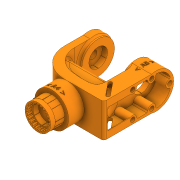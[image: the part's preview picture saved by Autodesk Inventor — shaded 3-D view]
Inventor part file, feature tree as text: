
AUTODESK INVENTOR PART (.ipt)
format: ipt  version: 2020 (Build 240168000, 168)  size: 2,288,128 bytes
history: native  units: in
note: dims shown in document units (in); Inventor stores cm internally (conversion verified against a paired STEP export)
features: sketch x47, extrude x43, projected_geometry x37, fillet x10, chamfer x9, plane x8, emboss x3
ambient origin geometry x8: Origin, YZ Plane, XZ Plane, XY Plane, X Axis, Y Axis, Z Axis, Center Point
bodies: Solid1 (feature_tree)
feature tree (157):
  extrude  "Extrusion1"  Depth=2.0472in
  extrude  "Extrusion2"  Depth=1.1063in
  chamfer  "Chamfer2"  Distance=0.5591in
  extrude  "Extrusion4"  Depth=0.0157in
  extrude  "Extrusion7"  Depth=0.2756in TaperAngle=0.0deg
  chamfer  "Chamfer4"  Distance=0.0394in
  extrude  "Extrusion8"  Depth=0.0157in
  sketch  "Sketch12"  dims[d39=1.4567in d57=0.0394in d58=0.0in]
  plane  "Work Plane1"
  sketch  "Sketch13"  dims[d59=0.315in d60=0.125in d61=0.0137in d67=0.0157in]
  extrude  "Extrusion10"  Depth=0.0394in TaperAngle=0.0deg
  extrude  "Extrusion11"  Depth=0.0866in
  chamfer  "Chamfer5"  Distance=9.4488in Angle=360.0deg
  extrude  "Extrusion12"  Depth=0.2756in TaperAngle=0.0deg
  plane  "Work Plane2"
  extrude  "Extrusion13"  Depth=0.315in
  plane  "Work Plane3"
  extrude  "Extrusion14"  Depth=1.0236in
  extrude  "Extrusion15"  Depth=0.8858in
  extrude  "Extrusion16"  Depth=0.3937in
  extrude  "Extrusion17"  Depth=1.378in
  sketch  "Sketch21"  dims[d107=0.315in d108=0.0in d109=0.315in d110=0.125in d111=0.0137in]
  extrude  "Extrusion19"  Depth=0.5906in
  sketch  "Sketch23"  dims[d112=1.0in d113=0.0in d114=1.0236in]
  extrude  "Extrusion20"  Depth=0.1575in TaperAngle=0.0deg
  extrude  "Extrusion21"  Depth=0.1575in TaperAngle=0.0deg
  extrude  "Extrusion22"  Depth=4.2323in
  extrude  "Extrusion23"  Depth=0.1575in
  extrude  "Extrusion24"  Depth=1.1024in
  extrude  "Extrusion25"  Depth=0.4921in
  extrude  "Extrusion26"  Depth=0.75in
  extrude  "Extrusion27"  Depth=0.2165in TaperAngle=0.0deg
  extrude  "Extrusion28"  Depth=0.1575in
  extrude  "Extrusion29"  Depth=0.1575in
  plane  "Work Plane4"
  extrude  "Extrusion30"  Depth=0.3937in TaperAngle=0.0deg
  fillet  "Fillet1"  Radius=0.3937in
  fillet  "Fillet2"  Radius=0.315in
  extrude  "Extrusion31"  Depth=0.315in TaperAngle=0.0deg
  extrude  "Extrusion32"  Depth=0.315in TaperAngle=0.0deg
  extrude  "Extrusion33"  Depth=0.3937in TaperAngle=0.0deg
  fillet  "Fillet3"  Radius=0.2165in
  extrude  "Extrusion34"  Depth=0.4724in
  chamfer  "Chamfer6"  Distance=0.2756in
  chamfer  "Chamfer7"  Distance=0.0394in
  extrude  "Extrusion35"  Depth=0.0394in
  extrude  "Extrusion36"  Depth=0.1575in TaperAngle=0.0deg
  fillet  "Fillet5"  Radius=0.1575in
  extrude  "Extrusion38"  Depth=0.315in
  extrude  "Extrusion39"  Depth=0.0157in
  extrude  "Extrusion40"  Depth=1.0in TaperAngle=0.0deg
  extrude  "Extrusion41"  Depth=0.3937in
  chamfer  "Chamfer8"  Distance=0.3937in
  extrude  "Extrusion42"  Depth=0.1575in
  plane  "Work Plane6"
  emboss  "Emboss1"
  emboss  "Emboss2"
  plane  "Work Plane7"
  emboss  "Emboss3"
  extrude  "Extrusion43"  Depth=0.1181in
  fillet  "Fillet9"  Radius=1.0039in
  chamfer  "Chamfer10"  Distance=0.0984in
  extrude  "Extrusion44"  Depth=0.0394in
  extrude  "Extrusion45"  Depth=0.0394in
  fillet  "Fillet12"  Radius=0.1181in
  fillet  "Fillet13"  Radius=0.2047in
  plane  "Work Plane8"
  extrude  "Extrusion46"  Depth=0.0394in
  plane  "Work Plane9"
  extrude  "Extrusion47"  TaperAngle=0.0deg  [1 undecoded]
  fillet  "Fillet14"  Radius=0.0787in
  extrude  "Extrusion48"  Depth=0.0394in
  extrude  "Extrusion49"  Depth=0.0394in
  chamfer  "Chamfer11"  Distance=0.0787in
  chamfer  "Chamfer12"  Distance=0.2756in
  fillet  "Fillet15"  Radius=0.2756in
  fillet  "Fillet16"  Radius=0.4724in
  sketch  "Sketch1"  dims[d0=0.6299in d1=2.0472in]
  sketch  "Sketch2"  dims[d2=0.9449in d3=0.0in d4=1.1063in]
  sketch  "Sketch4"  dims[d5=1.5748in d6=0.5591in d7=0.0in]
  sketch  "Sketch8"  dims[d11=0.5591in d12=0.125in d13=0.0137in d25=0.0157in]
  projected_geometry  "Projected Loop2"
  sketch  "Sketch10"  dims[d26=6.2992in d28=360.0deg d30=0.2756in d31=0.0in]
  sketch  "Sketch14"  dims[d68=4.7244in d70=360.0deg d72=0.0394in d73=0.0in]
  sketch  "Sketch15"  dims[d83=0.0591in d84=0.0866in]
  projected_geometry  "Projected Loop4"
  sketch  "Sketch16"  dims[d85=0.0827in]
  sketch  "Sketch17"  dims[d86=0.0827in]
  projected_geometry  "Projected Loop5"
  sketch  "Sketch18"  dims[d87=0.0827in d88=9.4488in d90=360.0deg]
  projected_geometry  "Projected Loop6"
  projected_geometry  "Projected Loop7"
  sketch  "Sketch19"  dims[d92=0.2756in]
  projected_geometry  "Projected Loop8"
  projected_geometry  "Projected Loop9"
  sketch  "Sketch20"  dims[d94=9.4488in d95=0.0827in d96=0.0827in d97=0.0827in d98=360.0deg d105=0.2756in d106=0.0in]
  projected_geometry  "Projected Loop10"
  projected_geometry  "Projected Loop11"
  projected_geometry  "Projected Loop12"
  projected_geometry  "Projected Loop13"
  sketch  "Sketch25"  dims[d115=0.7874in d117=0.8858in]
  sketch  "Sketch26"  dims[d118=2.7559in d119=0.3937in]
  projected_geometry  "Projected Loop16"
  projected_geometry  "Projected Loop17"
  sketch  "Sketch27"  dims[d120=0.5906in d121=1.378in]
  projected_geometry  "Projected Loop18"
  projected_geometry  "Projected Loop19"
  sketch  "Sketch28"  dims[d123=3.4941in d124=0.5906in]
  projected_geometry  "Projected Loop20"
  projected_geometry  "Projected Loop21"
  sketch  "Sketch29"  dims[d126=1.9685in d129=0.1575in d130=0.0in]
  projected_geometry  "Projected Loop22"
  projected_geometry  "Projected Loop23"
  sketch  "Sketch30"  dims[d131=-2.0472in d132=0.1575in d133=0.0in]
  projected_geometry  "Projected Loop24"
  sketch  "Sketch31"  dims[d134=2.126in d136=4.2323in]
  sketch  "Sketch32"  dims[d137=0.1575in d138=0.1575in]
  sketch  "Sketch34"  dims[d139=0.4921in d140=0.0in d141=1.1024in]
  projected_geometry  "Projected Loop25"
  sketch  "Sketch35"  dims[d142=1.1614in d143=0.4921in]
  sketch  "Sketch36"  dims[d144=0.3445in d145=0.75in]
  projected_geometry  "Projected Loop26"
  sketch  "Sketch37"  dims[d146=0.1575in d147=0.0in d148=0.2165in d149=0.0in]
  projected_geometry  "Projected Loop27"
  sketch  "Sketch38"  dims[d152=1.0039in d153=0.0in d154=0.1575in]
  projected_geometry  "Projected Loop28"
  sketch  "Sketch39"  dims[d155=0.1575in d160=1.1811in]
  projected_geometry  "Projected Loop29"
  sketch  "Sketch40"  dims[d161=0.1969in d162=0.0in d163=0.315in d164=0.0in d165=0.3937in d166=0.0in d167=0.315in d168=0.0in]
  sketch  "Sketch41"  dims[d169=0.315in d170=0.0in d171=0.315in d172=0.0in]
  projected_geometry  "Projected Loop30"
  sketch  "Sketch43"  dims[d173=0.315in d174=0.0in d175=0.315in d176=0.0in]
  projected_geometry  "Projected Loop31"
  sketch  "Sketch44"  dims[d177=1.1024in d178=0.3937in d179=0.0in d180=0.2165in d181=0.0in]
  sketch  "Sketch45"  dims[d183=-0.0197in d184=0.4724in d185=0.2756in d186=0.0in]
  sketch  "Sketch46"  dims[d187=0.5512in]
  projected_geometry  "Projected Loop32"
  sketch  "Sketch47"  dims[d188=0.2165in d189=0.0394in d190=0.0in]
  projected_geometry  "Projected Loop33"
  sketch  "Sketch48"  dims[d191=0.0394in d192=0.0in d193=0.001in]
  sketch  "Sketch49"  dims[d194=0.001in d195=1.0in d196=0.0in d197=0.1575in]
  sketch  "Sketch50"  dims[d198=1.0in d199=0.0in d200=0.315in d201=0.125in d202=0.0137in]
  sketch  "Sketch52"  dims[d203=0.315in d204=0.125in d205=0.0137in d206=0.0157in]
  sketch  "Sketch53"  dims[d207=2.3622in d209=360.0deg d211=1.0in d212=0.0in]
  projected_geometry  "Projected Loop35"
  projected_geometry  "Projected Loop36"
  projected_geometry  "Projected Loop37"
  projected_geometry  "Projected Loop38"
  projected_geometry  "Projected Loop39"
  sketch  "Sketch54"  dims[d213=1.0in d214=0.0in d221=0.1969in d222=0.3937in d223=0.0in]
  projected_geometry  "Projected Loop40"
  sketch  "Sketch56"  dims[d224=0.1575in d225=0.0787in]
  sketch  "Sketch57"  dims[d226=0.1969in d227=0.0in d229=0.1181in d230=1.0039in]
  sketch  "Sketch59"  dims[d231=0.4134in]
  projected_geometry  "Projected Loop41"
  sketch  "Sketch60"  dims[d232=0.5118in d233=0.0984in d235=0.0197in d236=0.1181in d237=0.1181in d238=0.2047in d239=0.2047in d240=0.0in d241=0.0in d243=0.0787in d244=0.0787in d251=0.0787in d252=0.0787in d253=0.2756in d254=0.4724in d255=0.2756in d256=0.4724in d257=0.2756in d258=0.4724in d259=0.2756in d260=0.4724in d261=0.1575in d262=0.0in d263=0.0787in d264=0.125in d265=45.0deg d266=1.0in d267=0.0in d269=0.0394in d270=0.0in d271=0.0394in d272=0.0in d273=0.0394in d274=0.0in d275=0.0039in d276=0.0787in d277=1.0in d278=0.0in d279=0.122in d282=0.1378in d283=0.2047in d288=0.0394in d289=0.125in d290=45.0deg d291=0.5709in d292=0.0in d293=0.2835in d294=0.0in d295=0.2361in d296=0.0315in d297=1.1811in d298=0.315in d299=0.0984in d300=0.0in d301=0.0984in d302=0.0984in d303=0.0in d304=0.0256in d305=0.2559in d306=0.0in d307=0.2559in d308=0.0in d309=0.1181in d310=0.1969in d311=45.0deg d312=0.1181in d313=0.1969in d314=45.0deg d315=0.1575in d316=0.0394in]
  projected_geometry  "Projected Loop42"
note: 1 required parameter value undecoded (feature->parameter linkage not recoverable at this tier; creation-order binding heuristic only, values carry confidence <= 0.55)
